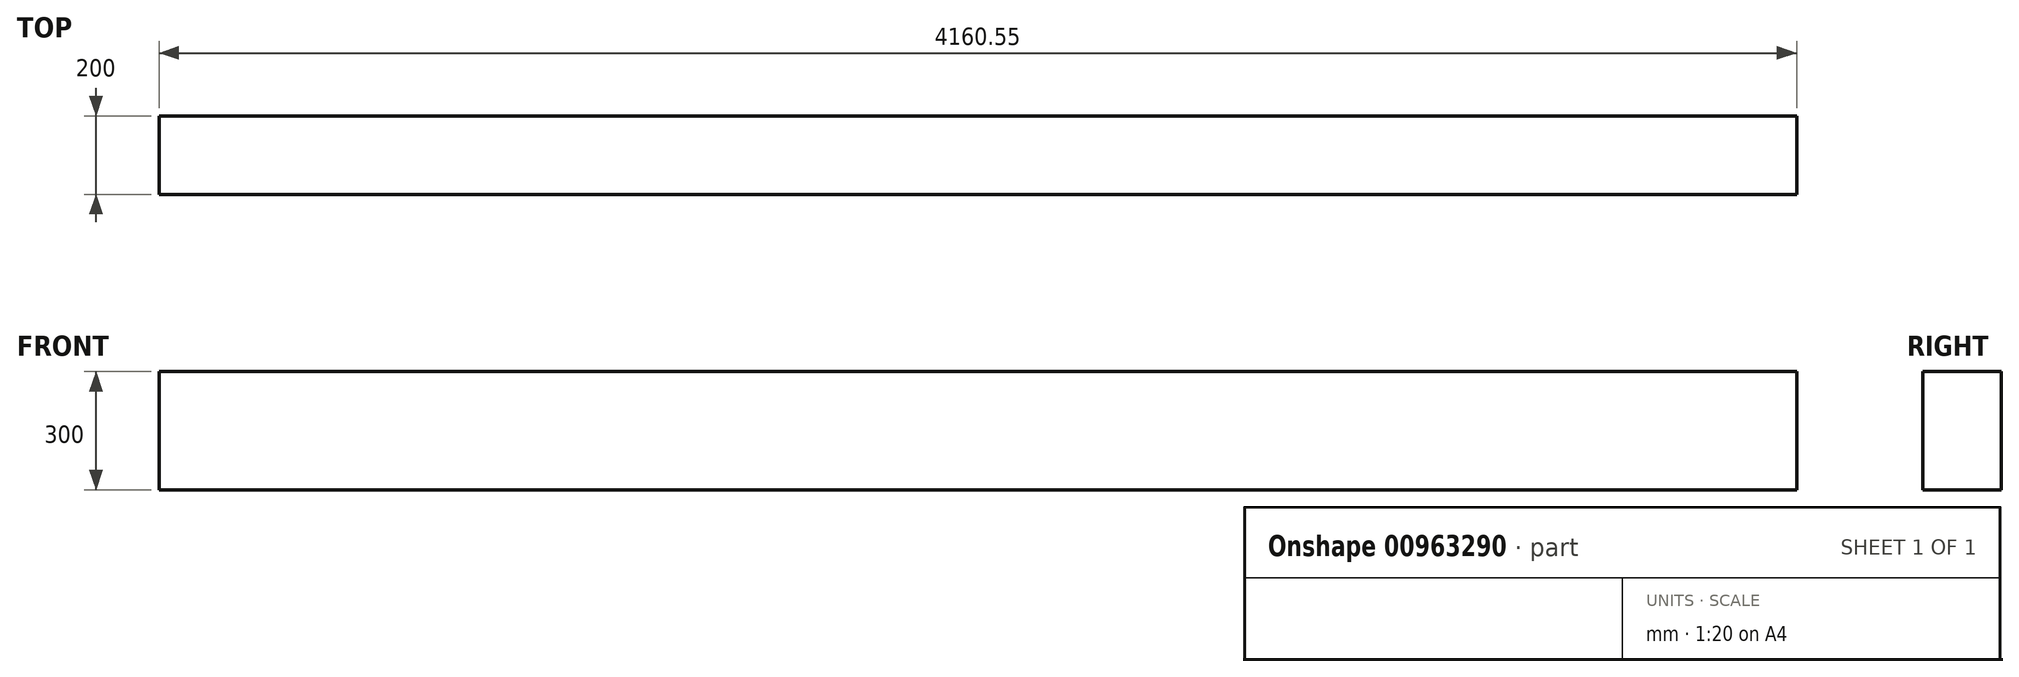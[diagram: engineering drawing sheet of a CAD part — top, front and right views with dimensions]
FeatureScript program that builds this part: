
annotation { "Feature Type Name" : "Feature", "Feature Type Description" : "" }
export const myFeature = defineFeature(function(context is Context, id is Id, definition is map)
    precondition{}
    {
        {
            var Q0;
            Q0=qCreatedBy(makeId("Right.planeOp"),FACE);
            var sketch = newSketch(context, id + "F0", { "sketchPlane" : qUnion([Q0])});
            skLineSegment(sketch, "E0.bottom", {"start": v(100, 0) * mm, "end": v(-100, 0) * mm});
            skLineSegment(sketch, "E0.top", {"start": v(100, 300) * mm, "end": v(-100, 300) * mm});
            skLineSegment(sketch, "E0.left", {"start": v(100, 0) * mm, "end": v(100, 300) * mm});
            skLineSegment(sketch, "E0.right", {"start": v(-100, 0) * mm, "end": v(-100, 300) * mm});
            skPoint(sketch, "E0.middle", {"position": v(0, 150) * mm});
            skSolve(sketch);
        }
        {
            var Q0;
            Q0=makeQuery(id+"F0.imprint","IMPRINT",FACE,{"disambiguationData":[TD([[makeQuery(id+"F0.imprint","IMPRINT",EDGE,{"derivedFrom":sQuery(id+"F0.wireOp",EDGE,"E0.bottom")}),-1.0]])]});
            extrude(context, id + "F1", {"entities" : qUnion([Q0]), "depth" : 4160.55 * mm, "offsetDistance" : 25 * mm});
        }
    });
